# Revit family: Resideo_TableStand_Evohome_ATF800a
name_source: partatom
category: Electrical Fixtures
units: mm (PartAtom-declared; Revit-internal decimal feet)

## family parameters
Cut with Voids When Loaded = No
Host = Face
Maintain Annotation Orientation = No
OmniClass Number = 23.75.65.11.11
OmniClass Title = Heating Controllers
Part Type = Normal
Room Calculation Point = No
Round Connector Dimension = Use Diameter
Shared = No

## types (1)
- ATF800
    Assembly Code = D3060
    AssetType = Fixed
    BIMObjectName = Resideo_TableStand_Evohome_ATF800
    ClassificationName = Uniclass2015
    Cost = 0 $
    Default Elevation = 0 mm  [stored 0 ft]
    Description = EVOHOME TABLE STAND
    DocumentationCertificates = https://www.bimstore.co
    DocumentationInstallationGuide = https://www.bimstore.co
    DocumentationLiterature = https://www.bimstore.co
    DocumentationMaintenance = https://www.bimstore.co
    DocumentationTechnical = https://www.bimstore.co
    DurationUnit = Years
    ExpectedLife = 0
    IfcExportAs = IfcBuildingElementProxy
    IfcExportType = USERDEFINED
    Keynote = W
    Manufacturer = Resideo
    ManufacturerName = Resideo
    Model = ATF800
    ModelNumber = ATF800
    ModelReference = EVOHOME TABLE STAND
    NBSDescription = Room temperature sensors
    NominalDepth = 60 mm  [stored 0.19685 ft]
    NominalHeight = 97 mm  [stored 0.318241 ft]
    NominalLength = 104 mm
    PrimaryMaterial = Resideo - Plastic - White
    ProductionYear = 2022
    Size = 60mm (D) x 97mm (H) x 104mm (L)
    Type Comments = EVOHOME TABLE STAND
    TypeName = ATF800 - EVOHOME TABLE STAND
    URL = https://www.resideo.com
    WarrantyDurationLabor = 0
    WarrantyDurationParts = 0
    WarrantyDurationUnit = Years
    WarrantyGuarantorLabor = https://www.resideo.com
    WarrantyGuarantorParts = https://www.resideo.com
    _BSBibleVersion = 16
    _BimSpecGuid = 0
    _CurrentRevision = 1
    _DistributedBy = https://www.bimstore.co
    _ObjectUserGuide = https://www.bimstore.co

note: [stored X ft] marks values corroborated as IEEE doubles in the binary element streams (Revit-internal decimal feet)

## geometry (parser evidence)
native form markers: Sweep x2
no freeform markers — native parametric forms only
